# Revit family: 28_SB_NL_Delft_Profielen_155R_840
name_source: partatom
category: Structural Framing
revit_build: Autodesk Revit 2016 (Build: 20161004_0715(x64)
units: mm (PartAtom-declared; Revit-internal decimal feet)

## family parameters
Always export as geometry = No
Always vertical = Yes
Cut with Voids When Loaded = No
Material for Model Behavior = Other
OmniClass Number = 23.25.30.11.14.14
OmniClass Title = Beams
Section Shape = Not Defined
Shared = No
Show family pre-cut in plan views = Yes

## types (1)
- 155R_840
    Assembly Code = 28.31
    BIM4ALL B.V. = www.bim4all.com
    Constructieve kenmerken = -
    Datum = 13-04-2018
    Description = 155R/840
    Dikte = 1 mm  [stored 0.00328084 ft]
    Duurzaamheid = Verzinkt Z-275 gr./m2 of interieur coating 15mu/BC
    Fabricage = Warmdakplaten Delft 155R/840 én EN 1090-2
    Manufacturer = Delft profielen b.v.
    Materiaal = S320D GD
    Maximale plaatlengte = 25000 mm
    Minimale overlap = 100 mm  [stored 0.328084 ft]
    Minimale plaatlengte = 1500 mm
    Norm = NEN-EN 1090-1: 2009 + A1:2011
    Ontwerp = NPD
    Radioactieve straling = NPD
    Reactie op bbrand = Klasse A1
    Toleranties op vorm en afmetingen = Tolerantieklasse D1 volgens EN 1090-2
    URL = www.delftprofielen.nl
    Vrijkomen van cadium = NPD

note: [stored X ft] marks values corroborated as IEEE doubles in the binary element streams (Revit-internal decimal feet)

## geometry (parser evidence)
native form markers: Sweep x2
no freeform markers — native parametric forms only
